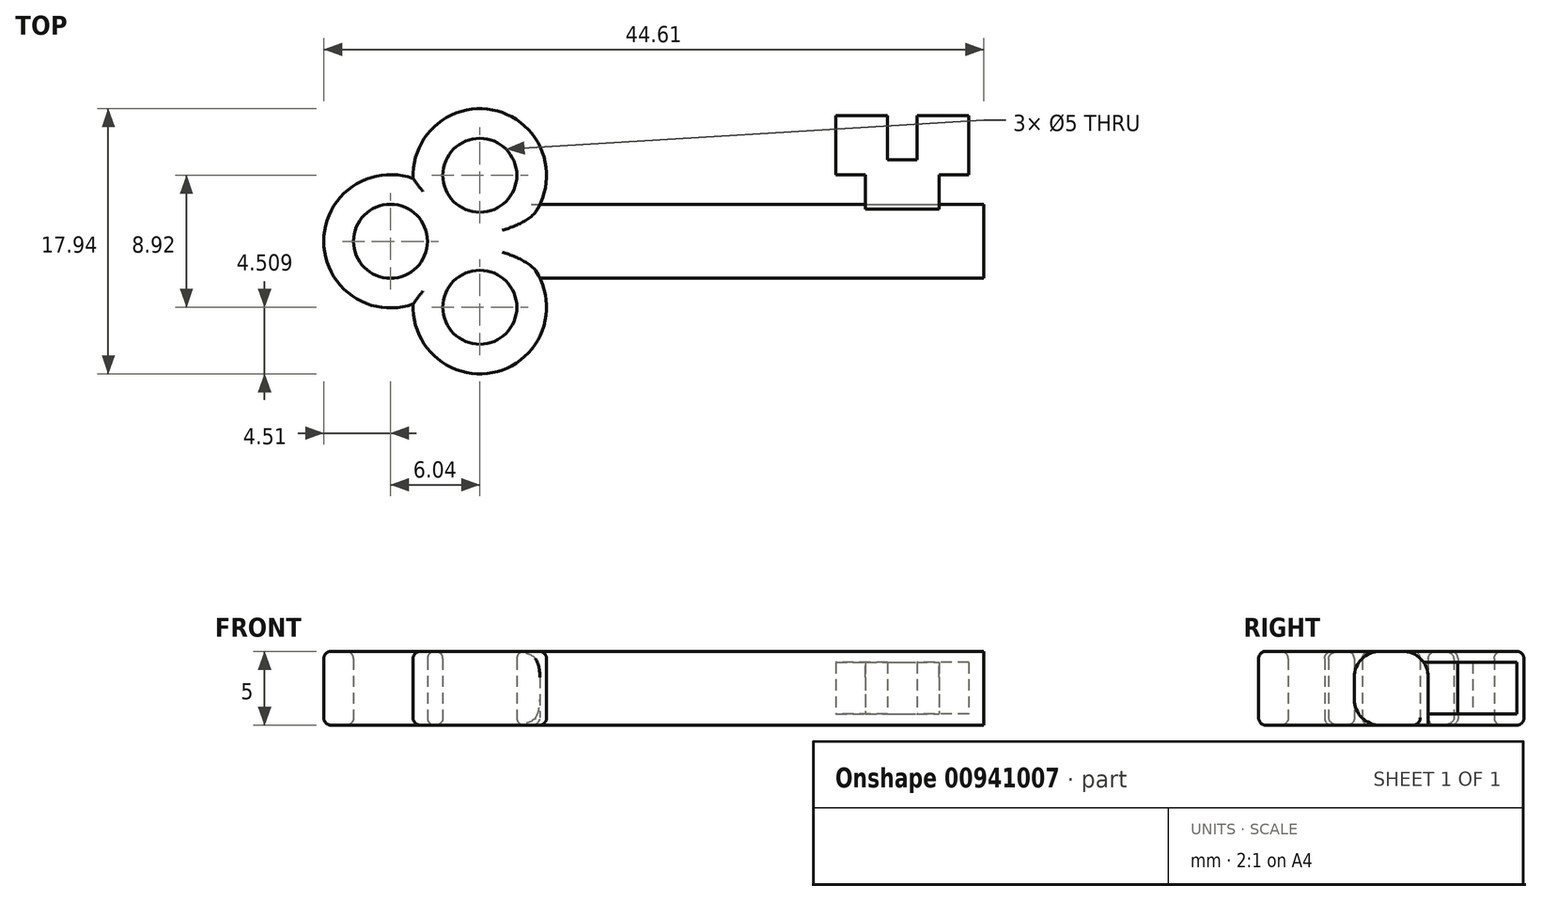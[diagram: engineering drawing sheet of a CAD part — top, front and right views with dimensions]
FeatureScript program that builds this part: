
annotation { "Feature Type Name" : "Feature", "Feature Type Description" : "" }
export const myFeature = defineFeature(function(context is Context, id is Id, definition is map)
    precondition{}
    {
        {
            var Q0;
            Q0=qCreatedBy(makeId("Top.planeOp"),FACE);
            var sketch = newSketch(context, id + "F0", { "sketchPlane" : qUnion([Q0])});
            skCircle(sketch, "E0", {"center": v(13, -25.24) * mm, "radius": 2.5 * mm});
            skCircle(sketch, "E1", {"center": v(13, -16.32) * mm, "radius": 2.5 * mm});
            skLineSegment(sketch, "E2", {"start": v(13, -25.24) * mm, "end": v(13, -16.32) * mm, "construction": true});
            skPoint(sketch, "E3.startSnap0", {"position": v(13, -20.78) * mm});
            skArc(sketch, "E4", {"start": v(8.5, -25.02) * mm, "mid": v(15.86, -28.72) * mm, "end": v(13.66, -20.78) * mm});
            skLineSegment(sketch, "E5", {"start": v(12.34, -20.78) * mm, "end": v(12.34, -20.78) * mm});
            skArc(sketch, "E6.trimOffspring", {"start": v(8.5, -16.54) * mm, "mid": v(2.45, -20.78) * mm, "end": v(8.5, -25.02) * mm});
            skArc(sketch, "E7.trimOffspring", {"start": v(13.66, -20.78) * mm, "mid": v(15.86, -12.84) * mm, "end": v(8.5, -16.54) * mm});
            skLineSegment(sketch, "E8", {"start": v(17.06, -23.28) * mm, "end": v(47.06, -23.28) * mm});
            skLineSegment(sketch, "E9", {"start": v(17.06, -18.28) * mm, "end": v(47.06, -18.28) * mm});
            skLineSegment(sketch, "E10", {"start": v(17.06, -23.28) * mm, "end": v(17.06, -18.28) * mm, "construction": true});
            skLineSegment(sketch, "E11", {"start": v(47.06, -23.28) * mm, "end": v(47.06, -18.28) * mm});
            skLineSegment(sketch, "E12", {"start": v(46.06, -16.28) * mm, "end": v(46.06, -12.28) * mm});
            skLineSegment(sketch, "E13", {"start": v(46.06, -12.28) * mm, "end": v(42.56, -12.28) * mm});
            skLineSegment(sketch, "E14", {"start": v(37.06, -12.28) * mm, "end": v(37.06, -16.28) * mm});
            skLineSegment(sketch, "E15", {"start": v(40.56, -12.28) * mm, "end": v(40.56, -15.28) * mm});
            skLineSegment(sketch, "E16", {"start": v(40.56, -15.28) * mm, "end": v(42.56, -15.28) * mm});
            skLineSegment(sketch, "E17", {"start": v(42.56, -15.28) * mm, "end": v(42.56, -12.28) * mm});
            skLineSegment(sketch, "E18", {"start": v(37.06, -16.28) * mm, "end": v(39.06, -16.28) * mm});
            skLineSegment(sketch, "E19", {"start": v(39.06, -16.28) * mm, "end": v(39.06, -18.28) * mm});
            skLineSegment(sketch, "E20.trimOffspring", {"start": v(40.56, -12.28) * mm, "end": v(37.06, -12.28) * mm});
            skLineSegment(sketch, "E21", {"start": v(46.06, -16.28) * mm, "end": v(44.06, -16.28) * mm});
            skLineSegment(sketch, "E22", {"start": v(44.06, -16.28) * mm, "end": v(44.06, -18.28) * mm});
            skPoint(sketch, "E23.orphan", {"position": v(46.06, -18.28) * mm});
            skLineSegment(sketch, "E24", {"start": v(46.06, -16.28) * mm, "end": v(46.06, -18.28) * mm, "construction": true});
            skCircle(sketch, "E25", {"center": v(6.96, -20.78) * mm, "radius": 2.5 * mm});
            skSolve(sketch);
        }
        {
            var Q0;
            {var subQ0=sQuery(id+"F0.wireOp",EDGE,"E8");Q0=makeQuery(id+"F0.imprint","IMPRINT",FACE,{"disambiguationData":[TD([[makeQuery(id+"F0.imprint","IMPRINT",EDGE,{"derivedFrom":subQ0}),1.0]])]});}
            var Q1;
            Q1=makeQuery(id+"F0.imprint","IMPRINT",FACE,{"disambiguationData":[TD([[makeQuery(id+"F0.imprint","IMPRINT",EDGE,{"derivedFrom":sQuery(id+"F0.wireOp",EDGE,"E0")}),-1.0]])]});
            extrude(context, id + "F1", {"entities" : qUnion([Q0, Q1]), "depth" : 5 * mm, "offsetDistance" : 25 * mm});
        }
        {
            var Q0;
            Q0=makeQuery(id+"F0.imprint","IMPRINT",FACE,{"disambiguationData":[TD([[makeQuery(id+"F0.imprint","IMPRINT",EDGE,{"derivedFrom":sQuery(id+"F0.wireOp",EDGE,"E12")}),1.0]])]});
            extrude(context, id + "F2", {"entities" : qUnion([Q0]), "operationType" : NewBodyOperationType.ADD, "depth" : 4.25 * mm, "offsetDistance" : 25 * mm});
        }
        {
            var Q0;
            Q0=makeQuery(id+"F2.opExtrude","SWEPT_FACE",FACE,{"disambiguationData":[OSD([sQuery(id+"F0.wireOp",EDGE,"E12")])]});
            var sketch = newSketch(context, id + "F3", { "sketchPlane" : qUnion([Q0])});
            skLineSegment(sketch, "E26.bottom", {"start": v(-11.46, 0.75) * mm, "end": v(-18.28, 0.75) * mm});
            skLineSegment(sketch, "E26.top", {"start": v(-11.46, 0) * mm, "end": v(-18.28, 0) * mm});
            skLineSegment(sketch, "E26.left", {"start": v(-11.46, 0.75) * mm, "end": v(-11.46, 0) * mm});
            skLineSegment(sketch, "E26.right", {"start": v(-18.28, 0.75) * mm, "end": v(-18.28, 0) * mm});
            skSolve(sketch);
        }
        {
            var Q0;
            {var subQ0=sQuery(id+"F3.wireOp",EDGE,"E26.right");Q0=makeQuery(id+"F3.imprint","IMPRINT",FACE,{"disambiguationData":[TD([[makeQuery(id+"F3.imprint","IMPRINT",EDGE,{"derivedFrom":subQ0}),1.0]])]});}
            var Q1;
            {var subQ0=sQuery(id+"F3.wireOp",EDGE,"E26.left");Q1=makeQuery(id+"F3.imprint","IMPRINT",FACE,{"disambiguationData":[TD([[makeQuery(id+"F3.imprint","IMPRINT",EDGE,{"derivedFrom":subQ0}),-1.0]])]});}
            var Q2;
            {var subQ0=sQuery(id+"F3.wireOp",EDGE,"E26.bottom");var subQ1=sQuery(id+"F0.wireOp",EDGE,"E12");var subQ2=makeQuery(id+"F2.opExtrude","SWEPT_EDGE",EDGE,{"disambiguationData":[OSD([subQ1,sQuery(id+"F0.wireOp",EDGE,"E13")])]});var subQ3=makeQuery(id+"F3.imprint","INTERSECT",VERTEX,{"derivedFrom":[subQ2,subQ0]});Q2=makeQuery(id+"F3.imprint","IMPRINT",FACE,{"disambiguationData":[TD([[makeQuery(id+"F3.imprint","IMPRINT",EDGE,{"disambiguationData":[TD([[subQ3,-1.0]])],"derivedFrom":subQ0}),1.0]])]});}
            extrude(context, id + "F4", {"entities" : qUnion([Q0, Q1, Q2]), "operationType" : NewBodyOperationType.REMOVE, "oppositeDirection" : true, "depth" : 25 * mm, "offsetDistance" : 25 * mm});
        }
        {
            var Q0;
            Q0=makeQuery(id+"F1.opExtrude","CAP_EDGE",EDGE,{"disambiguationData":[OSD([sQuery(id+"F0.wireOp",EDGE,"E8")])],"isStart":false});
            var Q1;
            Q1=makeQuery(id+"F1.opExtrude","CAP_EDGE",EDGE,{"disambiguationData":[OSD([sQuery(id+"F0.wireOp",EDGE,"E9")])],"isStart":false});
            var Q2;
            Q2=makeQuery(id+"F1.opExtrude","CAP_EDGE",EDGE,{"disambiguationData":[OSD([sQuery(id+"F0.wireOp",EDGE,"E8")])],"isStart":true});
            var Q3;
            {var subQ2=sQuery(id+"F0.wireOp",EDGE,"E9");var subQ4=sQuery(id+"F0.wireOp",EDGE,"E11");var subQ6=sQuery(id+"F0.wireOp",EDGE,"E7.trimOffspring");var subQ8=makeQuery(id+"F1.opExtrude","CAP_EDGE",EDGE,{"disambiguationData":[OSD([subQ2])],"isStart":true});Q3=makeQuery(id+"F4.boolean.opBoolean","MERGE",EDGE,{"derivedFrom":[makeQuery(id+"F2.boolean.opBoolean","SPLIT",EDGE,{"disambiguationData":[TD([makeQuery(id+"F1.opExtrude","SWEPT_FACE",FACE,{"disambiguationData":[OSD([subQ6])]})])],"derivedFrom":subQ8}),makeQuery(id+"F2.boolean.opBoolean","SPLIT",EDGE,{"disambiguationData":[TD([makeQuery(id+"F1.opExtrude","SWEPT_FACE",FACE,{"disambiguationData":[OSD([subQ4])]})])],"derivedFrom":subQ8})],"fromTools":[makeQuery(id+"F4.opExtrude","SWEPT_EDGE",EDGE,{"disambiguationData":[OSD([sQuery(id+"F3.wireOp",EDGE,"E26.top"),sQuery(id+"F3.wireOp",EDGE,"E26.right")])]})]});}
            fillet(context, id + "F5", {"entities" : qUnion([Q0, Q1, Q2, Q3]), "radius" : 1.75 * mm, "tangentPropagation" : true, "allowEdgeOverflow" : false});
        }
        {
            var Q0;
            Q0=makeQuery(id+"F1.opExtrude","CAP_EDGE",EDGE,{"disambiguationData":[OSD([sQuery(id+"F0.wireOp",EDGE,"E4")])],"isStart":false});
            var Q1;
            Q1=makeQuery(id+"F1.opExtrude","CAP_EDGE",EDGE,{"disambiguationData":[OSD([sQuery(id+"F0.wireOp",EDGE,"E6.trimOffspring")])],"isStart":false});
            var Q2;
            Q2=makeQuery(id+"F1.opExtrude","CAP_EDGE",EDGE,{"disambiguationData":[OSD([sQuery(id+"F0.wireOp",EDGE,"E7.trimOffspring")])],"isStart":false});
            var Q3;
            Q3=makeQuery(id+"F1.opExtrude","CAP_EDGE",EDGE,{"disambiguationData":[OSD([sQuery(id+"F0.wireOp",EDGE,"E7.trimOffspring")])],"isStart":true});
            var Q4;
            Q4=makeQuery(id+"F1.opExtrude","CAP_EDGE",EDGE,{"disambiguationData":[OSD([sQuery(id+"F0.wireOp",EDGE,"E6.trimOffspring")])],"isStart":true});
            var Q5;
            Q5=makeQuery(id+"F1.opExtrude","CAP_EDGE",EDGE,{"disambiguationData":[OSD([sQuery(id+"F0.wireOp",EDGE,"E4")])],"isStart":true});
            var Q6;
            Q6=makeQuery(id+"F1.opExtrude","CAP_EDGE",EDGE,{"disambiguationData":[OSD([sQuery(id+"F0.wireOp",EDGE,"E1")])],"isStart":true});
            var Q7;
            Q7=makeQuery(id+"F1.opExtrude","CAP_EDGE",EDGE,{"disambiguationData":[OSD([sQuery(id+"F0.wireOp",EDGE,"4AlYVSM3-h1bt-zEst-GEy9-VrPurWV6PBEX")])],"isStart":true});
            var Q8;
            Q8=makeQuery(id+"F1.opExtrude","CAP_EDGE",EDGE,{"disambiguationData":[OSD([sQuery(id+"F0.wireOp",EDGE,"E0")])],"isStart":true});
            var Q9;
            Q9=makeQuery(id+"F1.opExtrude","CAP_EDGE",EDGE,{"disambiguationData":[OSD([sQuery(id+"F0.wireOp",EDGE,"E1")])],"isStart":false});
            var Q10;
            Q10=makeQuery(id+"F1.opExtrude","CAP_EDGE",EDGE,{"disambiguationData":[OSD([sQuery(id+"F0.wireOp",EDGE,"4AlYVSM3-h1bt-zEst-GEy9-VrPurWV6PBEX")])],"isStart":false});
            var Q11;
            Q11=makeQuery(id+"F1.opExtrude","CAP_EDGE",EDGE,{"disambiguationData":[OSD([sQuery(id+"F0.wireOp",EDGE,"E0")])],"isStart":false});
            var Q12;
            Q12=makeQuery(id+"F2.opExtrude","SWEPT_EDGE",EDGE,{"disambiguationData":[OSD([sQuery(id+"F0.wireOp",EDGE,"E9"),sQuery(id+"F0.wireOp",EDGE,"E19")])]});
            var Q13;
            Q13=makeQuery(id+"F2.opExtrude","SWEPT_EDGE",EDGE,{"disambiguationData":[OSD([sQuery(id+"F0.wireOp",EDGE,"E9"),sQuery(id+"F0.wireOp",EDGE,"E22")])]});
            var Q14;
            Q14=makeQuery(id+"F1.opExtrude","CAP_EDGE",EDGE,{"disambiguationData":[OSD([sQuery(id+"F0.wireOp",EDGE,"E25")])],"isStart":false});
            var Q15;
            Q15=makeQuery(id+"F1.opExtrude","CAP_EDGE",EDGE,{"disambiguationData":[OSD([sQuery(id+"F0.wireOp",EDGE,"E25")])],"isStart":true});
            fillet(context, id + "F6", {"entities" : qUnion([Q0, Q1, Q2, Q3, Q4, Q5, Q6, Q7, Q8, Q9, Q10, Q11, Q12, Q13, Q14, Q15]), "radius" : .5 * mm, "tangentPropagation" : true, "allowEdgeOverflow" : false});
        }
    });
